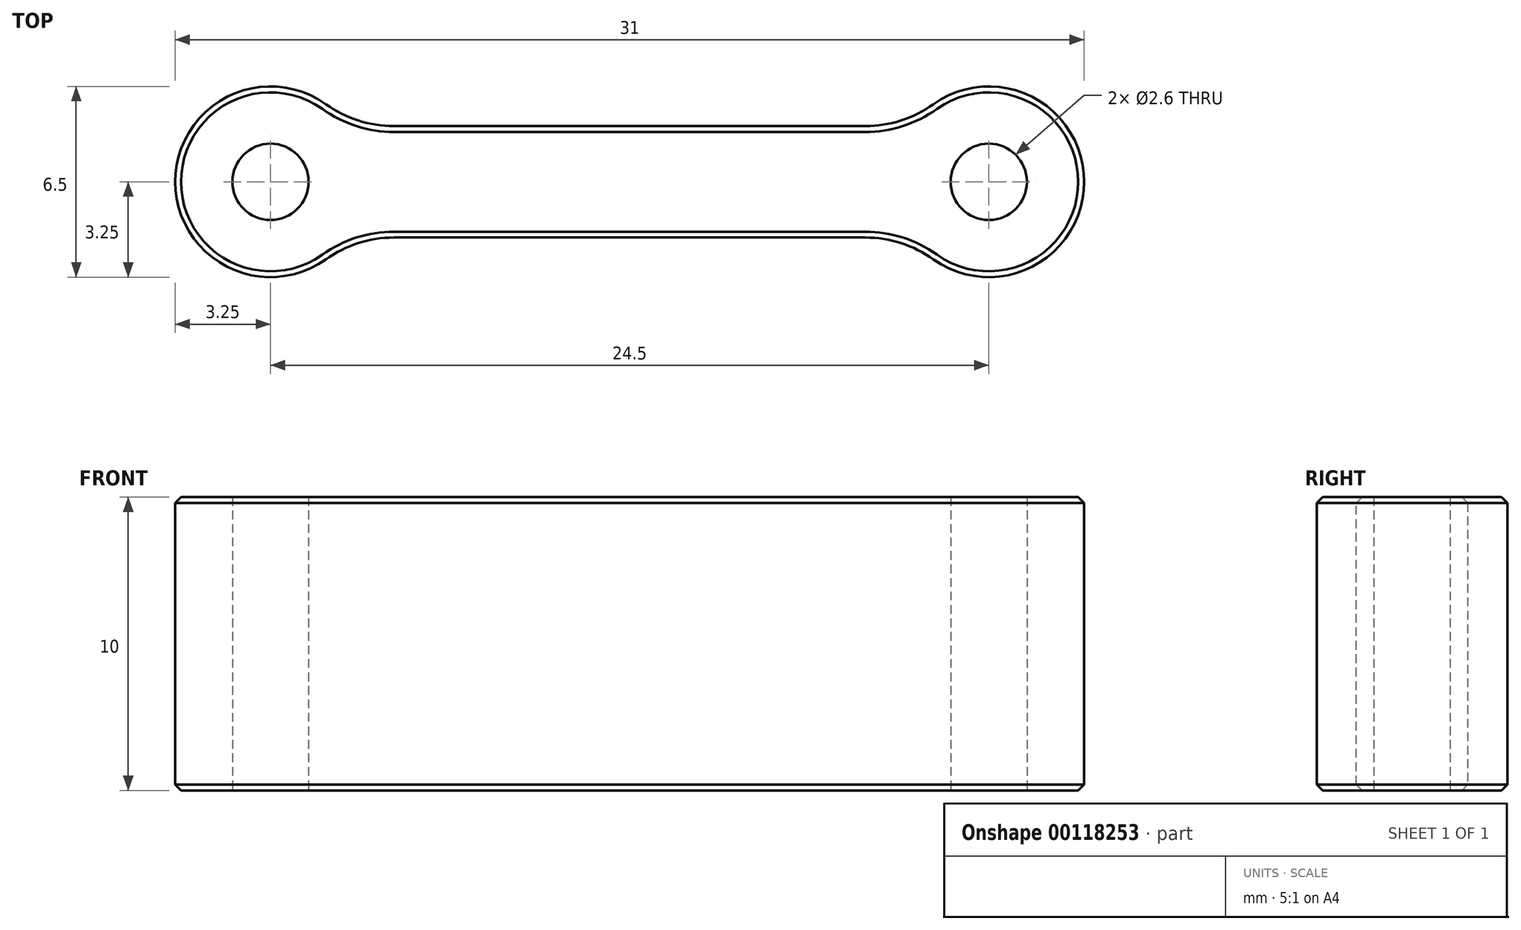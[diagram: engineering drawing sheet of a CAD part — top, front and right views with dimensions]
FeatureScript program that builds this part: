
annotation { "Feature Type Name" : "Feature", "Feature Type Description" : "" }
export const myFeature = defineFeature(function(context is Context, id is Id, definition is map)
    precondition{}
    {
        {
            var Q0;
            Q0=qCreatedBy(makeId("Top.planeOp"),FACE);
            var sketch = newSketch(context, id + "F0", { "sketchPlane" : qUnion([Q0])});
            skLineSegment(sketch, "E0.bottom", {"start": v(2.64, -1.9) * mm, "end": v(21.86, -1.9) * mm});
            skLineSegment(sketch, "E0.top", {"start": v(2.64, 1.9) * mm, "end": v(21.86, 1.9) * mm});
            skLineSegment(sketch, "E1", {"start": v(0, 0) * mm, "end": v(24.5, 0) * mm, "construction": true});
            skArc(sketch, "E2", {"start": v(21.86, 1.9) * mm, "mid": v(21.25, 0) * mm, "end": v(21.86, -1.9) * mm, "construction": true});
            skArc(sketch, "E3", {"start": v(21.86, -1.9) * mm, "mid": v(27.75, 0) * mm, "end": v(21.86, 1.9) * mm});
            skArc(sketch, "E4", {"start": v(2.64, 1.9) * mm, "mid": v(-3.25, 0) * mm, "end": v(2.64, -1.9) * mm});
            skArc(sketch, "E5", {"start": v(2.64, -1.9) * mm, "mid": v(3.25, 0) * mm, "end": v(2.64, 1.9) * mm, "construction": true});
            skSolve(sketch);
        }
        {
            var Q0;
            Q0 = qSketchRegion(id + "F0", true);
            extrude(context, id + "F1", {"entities" : qUnion([Q0]), "depth" : 10 * mm});
        }
        {
            var Q0;
            Q0=sQuery(id+"F0.wireOp",VERTEX,"E4.center");
            var Q1;
            Q1=sQuery(id+"F0.wireOp",VERTEX,"E3.center");
            var Q2;
            Q2=makeQuery(id+"F1.opExtrude","SWEPT_BODY",BODY,{"disambiguationData":[OSD([sQuery(id+"F0.wireOp",EDGE,"E0.bottom"),sQuery(id+"F0.wireOp",EDGE,"E0.top"),sQuery(id+"F0.wireOp",EDGE,"E3"),sQuery(id+"F0.wireOp",EDGE,"E4")])]});
            hole(context, id + "F2", {"style" : HoleStyle.SIMPLE, "endStyle" : HoleEndStyle.THROUGH, "oppositeDirection" : true, "holeDiameter" : 2.6 * mm, "tappedDepth" : 12 * mm, "tapClearance" : 3, "startFromSketch" : true, "locations" : qUnion([Q0, Q1]), "scope" : qUnion([Q2])});
        }
        {
            var Q0;
            Q0=makeQuery(id+"F1.opExtrude","SWEPT_EDGE",EDGE,{"disambiguationData":[OSD([sQuery(id+"F0.wireOp",EDGE,"E0.bottom"),sQuery(id+"F0.wireOp",EDGE,"E4")])]});
            var Q1;
            Q1=makeQuery(id+"F1.opExtrude","SWEPT_EDGE",EDGE,{"disambiguationData":[OSD([sQuery(id+"F0.wireOp",EDGE,"E0.bottom"),sQuery(id+"F0.wireOp",EDGE,"E3")])]});
            var Q2;
            Q2=makeQuery(id+"F1.opExtrude","SWEPT_EDGE",EDGE,{"disambiguationData":[OSD([sQuery(id+"F0.wireOp",EDGE,"E0.top"),sQuery(id+"F0.wireOp",EDGE,"E4")])]});
            var Q3;
            Q3=makeQuery(id+"F1.opExtrude","SWEPT_EDGE",EDGE,{"disambiguationData":[OSD([sQuery(id+"F0.wireOp",EDGE,"E0.top"),sQuery(id+"F0.wireOp",EDGE,"E3")])]});
            fillet(context, id + "F3", {"entities" : qUnion([Q0, Q1, Q2, Q3]), "radius" : 4 * mm, "tangentPropagation" : true, "allowEdgeOverflow" : false});
        }
        {
            var Q0;
            Q0=makeQuery(id+"F1.opExtrude","CAP_EDGE",EDGE,{"disambiguationData":[OSD([sQuery(id+"F0.wireOp",EDGE,"E0.top")])],"isStart":true});
            var Q1;
            Q1=makeQuery(id+"F1.opExtrude","CAP_EDGE",EDGE,{"disambiguationData":[OSD([sQuery(id+"F0.wireOp",EDGE,"E0.top")])],"isStart":false});
            chamfer(context, id + "F4", {"entities" : qUnion([Q0, Q1]), "width" : 0.2 * mm, "tangentPropagation" : true});
        }
    });
